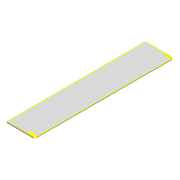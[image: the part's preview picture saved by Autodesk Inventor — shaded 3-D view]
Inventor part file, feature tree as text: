
AUTODESK INVENTOR PART (.ipt)
format: ipt  version: 2022 (Build 260153000, 153)  size: 122,368 bytes
history: native  units: mm
features: sketch x4, extrude x3, pattern_linear x1, plane x1, mirror x1, projected_geometry x1
ambient origin geometry x8: Origin, YZ Plane, XZ Plane, XY Plane, X Axis, Y Axis, Z Axis, Center Point
bodies: Solid1 (feature_tree)
feature tree (11):
  extrude  "Extrusion1"  Depth=100.0mm
  extrude  "Extrusion2"  Depth=6.0mm
  pattern_linear  "Rectangular Pattern1"  Spacing1=10.0mm  [1 undecoded]
  plane  "Work Plane1"
  extrude  "Extrusion3"  Depth=6.0mm
  mirror  "Mirror1"
  sketch  "Sketch4"  dims[d6=10.0mm d7=10.0mm d8=0.0mm d9=30.0mm d11=6.0mm d12=4.0mm d13=5.0mm d14=100.0mm d15=0.0mm]
  sketch  "Sketch1"  dims[d0=500.0mm d1=100.0mm]
  sketch  "Sketch2"  dims[d2=6.0mm d3=0.0mm d4=2.95mm]
  sketch  "Sketch3"  dims[d5=5.0mm]
  projected_geometry  "Projected Loop1"
note: 1 required parameter value undecoded (feature->parameter linkage not recoverable at this tier; creation-order binding heuristic only, values carry confidence <= 0.55)
